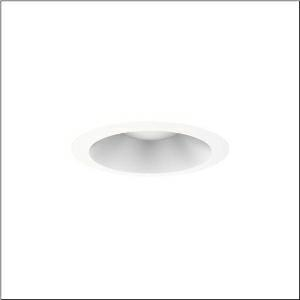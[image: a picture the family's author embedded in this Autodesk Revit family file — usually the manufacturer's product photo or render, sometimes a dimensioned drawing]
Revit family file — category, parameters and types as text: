
# Revit family: lunis_31_midi_51dn157g32
name_source: partatom
category: Lighting Fixtures
units: mm (PartAtom-declared; Revit-internal decimal feet)

## family parameters
Cut with Voids When Loaded = No
Host = Face
Light Source = No
Part Type = Normal
Room Calculation Point = No
Round Connector Dimension = Use Diameter
Shared = No

## types (1)
- Lunis 31 midi (1 x LED, 2000 lm, 17 W, 3000K)
    Apparent Load = 17 VA
    CIE Flux Codes = 89 99 100 100 100
    Color Rendering = 80
    Color Temperature = 3000K
    Default Elevation = 1800 mm
    Description = Lunis 31,  midi, downlight, light control with reflector, light emission: direct distribution, LED rated luminous flux: 2.050lm, light colour: 830, control gear: ECG, mains connection: 220..240V, AC, 50/60Hz, housing, white, protection rating (complete): IP20, insulation class (complete): insulation class II (safety insulation), certification: CE, packaging unit: 1 piece
    Height = 0 mm  [stored 0 ft]
    Lamp = 1 x LED
    Lamp Light Flux = 2000 lm
    Lamp Power = 17 W
    Lamp count = 1
    Length = 259 mm
    Luminous efficacy = 118 lm/W
    Manufacturer = Siteco
    ModVariant = No
    Model = 51DN157G32
    Mounting Place = Ceiling
    Mounting Type = Recessed
    Number of Poles = 1
    OnlyDefault = Yes
    Power Factor = 1
    Product Name = Lunis 31 midi
    Product group = downlight | ceiling recessed
    ProductGroupID = 402
    Protection Class = Protection class II
    Protection Degree = IP 20
    RLX_Detail_Level = 1
    RlxData = <blob elided: 23721 chars, md5=4d825483>
    Socket = socket
    Standby Power = 0 W
    System Light Flux = 2000 lm
    System Power = 17 W
    Type Comments = Product without accessories
    Type Image = l_1006711.jpg
    URL = http://relux.com
    VarID = ---
    Voltage = 0 V
    Weight = 0.00 kg
    Width = 0 mm  [stored 0 ft]

note: [stored X ft] marks values corroborated as IEEE doubles in the binary element streams (Revit-internal decimal feet)

## geometry (parser evidence)
native form markers: Blend x4, Sweep x12
no freeform markers — native parametric forms only
